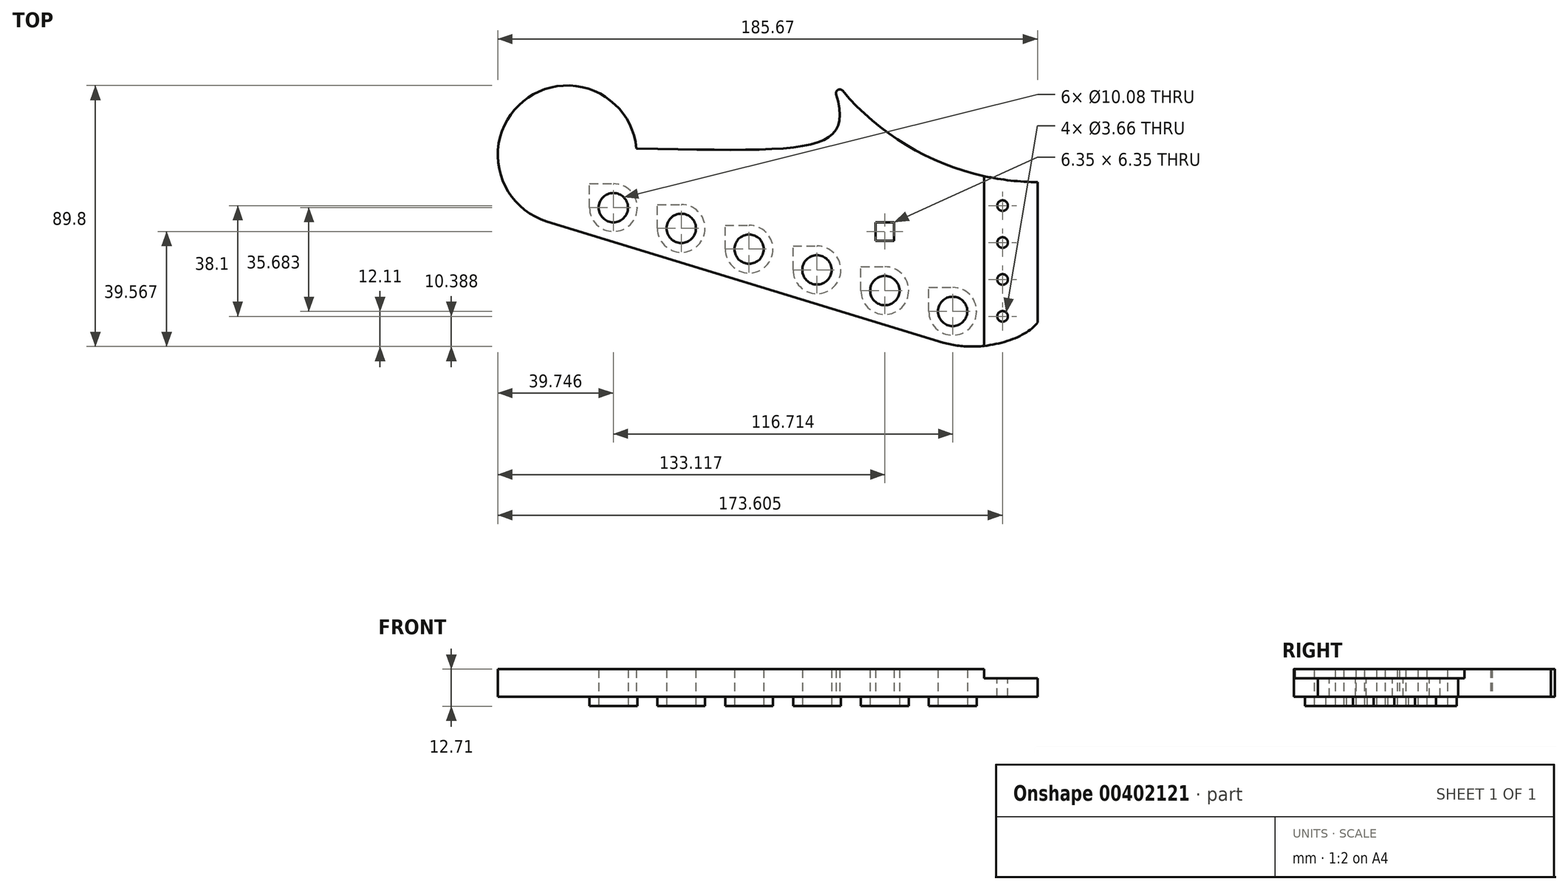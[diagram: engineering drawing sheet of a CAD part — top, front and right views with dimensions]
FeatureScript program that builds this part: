
annotation { "Feature Type Name" : "Feature", "Feature Type Description" : "" }
export const myFeature = defineFeature(function(context is Context, id is Id, definition is map)
    precondition{}
    {
        {
            var Q0;
            Q0=qCreatedBy(makeId("Top.planeOp"),FACE);
            var sketch = newSketch(context, id + "F0", { "sketchPlane" : qUnion([Q0])});
            skPoint(sketch, "E0", {"position": v(-185.67, 33.46) * mm});
            skLineSegment(sketch, "E1", {"start": v(0, 24.13) * mm, "end": v(0, -24.13) * mm});
            skCircle(sketch, "E2", {"center": v(-29.21, -20.32) * mm, "radius": 5.04 * mm});
            skLineSegment(sketch, "E3", {"start": v(0, 0) * mm, "end": v(0, 0) * mm});
            skPoint(sketch, "E3.endSnap0", {"position": v(0, 0) * mm});
            skCircle(sketch, "E4.1.0.0", {"center": v(-52.55, -13.18) * mm, "radius": 5.04 * mm});
            skCircle(sketch, "E4.2.0.0", {"center": v(-75.9, -6.05) * mm, "radius": 5.04 * mm});
            skCircle(sketch, "E4.3.0.0", {"center": v(-99.24, 1.09) * mm, "radius": 5.04 * mm});
            skCircle(sketch, "E4.4.0.0", {"center": v(-122.58, 8.23) * mm, "radius": 5.04 * mm});
            skCircle(sketch, "E4.5.0.0", {"center": v(-145.92, 15.36) * mm, "radius": 5.04 * mm});
            skLineSegment(sketch, "E4.direction1", {"start": v(-29.21, -20.32) * mm, "end": v(-52.55, -13.18) * mm, "construction": true});
            skLineSegment(sketch, "E5", {"start": v(-18.42, 26.22) * mm, "end": v(-18.41, -32.2) * mm});
            skLineSegment(sketch, "E6", {"start": v(-32.5, -31.06) * mm, "end": v(-168.76, 10.6) * mm});
            skLineSegment(sketch, "E7", {"start": v(-29.21, -20.32) * mm, "end": v(-32.5, -31.06) * mm, "construction": true});
            skFitSpline(sketch, "E8", {"points": [v(-32.5, -31.06) * mm, v(0, -24.13) * mm], "startDerivative": vector(36.44, -11.14) * mm, "endDerivative": vector(14.29, 19.05) * mm});
            skLineSegment(sketch, "E9", {"start": v(0, 0) * mm, "end": v(99.12, 0) * mm, "construction": true});
            skArc(sketch, "E10", {"start": v(-168.76, 10.6) * mm, "mid": v(-180.99, 19.25) * mm, "end": v(-185.67, 33.46) * mm});
            skLineSegment(sketch, "E11", {"start": v(-185.67, 33.46) * mm, "end": v(-185.67, 61.73) * mm, "construction": true});
            skArc(sketch, "E12", {"start": v(-137.98, 35.75) * mm, "mid": v(-162.91, 57.34) * mm, "end": v(-185.67, 33.46) * mm});
            skArc(sketch, "E13", {"start": v(-72.27, 62.33) * mm, "mid": v(-40.79, 34.43) * mm, "end": v(0, 24.13) * mm});
            skLineSegment(sketch, "E14", {"start": v(8.57, 3.57) * mm, "end": v(-99.24, 3.57) * mm, "construction": true});
            skLineSegment(sketch, "E15", {"start": v(8.57, -3.57) * mm, "end": v(-75.9, -3.57) * mm, "construction": true});
            skCircle(sketch, "E16", {"center": v(-75.9, -6.05) * mm, "radius": 2.48 * mm});
            skCircle(sketch, "E17", {"center": v(-99.24, 1.09) * mm, "radius": 2.48 * mm});
            skLineSegment(sketch, "E18", {"start": v(-99.24, 3.57) * mm, "end": v(-99.24, 1.09) * mm, "construction": true});
            skLineSegment(sketch, "E19", {"start": v(-75.9, -3.57) * mm, "end": v(-75.9, -6.05) * mm, "construction": true});
            skLineSegment(sketch, "E20", {"start": v(-137.98, 35.75) * mm, "end": v(-72.27, 62.33) * mm, "construction": true});
            skFitSpline(sketch, "E21", {"points": [v(-137.98, 35.75) * mm, v(-72.27, 62.33) * mm], "startDerivative": vector(194.61, -3.65) * mm, "endDerivative": vector(-37.72, 87.36) * mm});
            skCircle(sketch, "E22", {"center": v(-122.58, 8.23) * mm, "radius": 2.48 * mm});
            skCircle(sketch, "E23", {"center": v(-145.92, 15.36) * mm, "radius": 2.48 * mm});
            skLineSegment(sketch, "E24", {"start": v(-122.58, 8.23) * mm, "end": v(-122.58, 10.7) * mm});
            skLineSegment(sketch, "E25", {"start": v(-145.92, 15.36) * mm, "end": v(-145.92, 17.84) * mm});
            skLineSegment(sketch, "E26", {"start": v(-122.58, 10.7) * mm, "end": v(7.67, 10.7) * mm, "construction": true});
            skLineSegment(sketch, "E27", {"start": v(-145.92, 17.84) * mm, "end": v(21.7, 17.84) * mm, "construction": true});
            skSolve(sketch);
        }
        {
            var Q0;
            Q0=qSketchRegion(id+"F0",true);
            extrude(context, id + "F1", {"entities" : qUnion([Q0]), "depth" : 6.35 * mm});
        }
        {
            var Q0;
            Q0=makeQuery(id+"F0.imprint","IMPRINT",FACE,{"disambiguationData":[TD([[makeQuery(id+"F0.imprint","IMPRINT",EDGE,{"derivedFrom":sQuery(id+"F0.wireOp",EDGE,"E2")}),-1.0]])]});
            extrude(context, id + "F2", {"entities" : qUnion([Q0]), "operationType" : NewBodyOperationType.ADD, "depth" : 9.52 * mm});
        }
        {
            var Q0;
            Q0=makeQuery(id+"F1.opExtrude","CAP_FACE",FACE,{"disambiguationData":[OSD([sQuery(id+"F0.wireOp",EDGE,"4aa001a9-7916-4ac9-b611-f33505b9f3c5"),sQuery(id+"F0.wireOp",EDGE,"77602153-f705-4483-a7fc-31cc86b3ea61"),sQuery(id+"F0.wireOp",EDGE,"ee52411e-a9e7-4ef9-bd5f-1803b2297118"),sQuery(id+"F0.wireOp",EDGE,"E1"),sQuery(id+"F0.wireOp",EDGE,"E2"),sQuery(id+"F0.wireOp",EDGE,"E4.1.0.0"),sQuery(id+"F0.wireOp",EDGE,"E4.2.0.0"),sQuery(id+"F0.wireOp",EDGE,"E4.3.0.0"),sQuery(id+"F0.wireOp",EDGE,"E4.4.0.0"),sQuery(id+"F0.wireOp",EDGE,"E4.5.0.0"),sQuery(id+"F0.wireOp",EDGE,"05dfdfb5-9140-4733-bf36-b7656169c247"),sQuery(id+"F0.wireOp",EDGE,"fa98ec53-b239-455b-819f-4d27d42f24a3")])],"isStart":false});
            var sketch = newSketch(context, id + "F3", { "sketchPlane" : qUnion([Q0])});
            skPoint(sketch, "E28", {"position": v(-12.06, -22.04) * mm});
            skPoint(sketch, "E29", {"position": v(-12.06, 16.06) * mm});
            skPoint(sketch, "E30", {"position": v(-12.07, 3.36) * mm});
            skPoint(sketch, "E31", {"position": v(-12.06, -9.34) * mm});
            skLineSegment(sketch, "E32", {"start": v(0, -3) * mm, "end": v(-18.41, -3) * mm, "construction": true});
            skSolve(sketch);
        }
        {
            var Q0;
            Q0=sQuery(id+"F3.wireOp",VERTEX,"E29");
            var Q1;
            Q1=sQuery(id+"F3.wireOp",VERTEX,"E30");
            var Q2;
            Q2=sQuery(id+"F3.wireOp",VERTEX,"E31");
            var Q3;
            Q3=sQuery(id+"F3.wireOp",VERTEX,"E28");
            var Q4;
            Q4=makeQuery(id+"F1.opExtrude","SWEPT_BODY",BODY,{"disambiguationData":[OSD([sQuery(id+"F0.wireOp",EDGE,"4aa001a9-7916-4ac9-b611-f33505b9f3c5"),sQuery(id+"F0.wireOp",EDGE,"77602153-f705-4483-a7fc-31cc86b3ea61"),sQuery(id+"F0.wireOp",EDGE,"ee52411e-a9e7-4ef9-bd5f-1803b2297118"),sQuery(id+"F0.wireOp",EDGE,"E1"),sQuery(id+"F0.wireOp",EDGE,"E2"),sQuery(id+"F0.wireOp",EDGE,"E4.1.0.0"),sQuery(id+"F0.wireOp",EDGE,"E4.2.0.0"),sQuery(id+"F0.wireOp",EDGE,"E4.3.0.0"),sQuery(id+"F0.wireOp",EDGE,"E4.4.0.0"),sQuery(id+"F0.wireOp",EDGE,"E4.5.0.0"),sQuery(id+"F0.wireOp",EDGE,"05dfdfb5-9140-4733-bf36-b7656169c247"),sQuery(id+"F0.wireOp",EDGE,"fa98ec53-b239-455b-819f-4d27d42f24a3")])]});
            hole(context, id + "F4", {"style" : HoleStyle.SIMPLE, "endStyle" : HoleEndStyle.THROUGH, "standardTappedOrClearance" : lookupTablePath({ "standard" : "ANSI", "fit" : "Close", "size" : "#6", "type" : "Clearance" }), "standardBlindInLast" : lookupTablePath({ "fit" : "Close", "standard" : "ANSI", "size" : "#6", "type" : "Clearance" }), "holeDiameter" : 3.66 * mm, "startFromSketch" : true, "locations" : qUnion([Q0, Q1, Q2, Q3]), "scope" : qUnion([Q4]), "isTappedThrough" : true});
        }
        {
            var Q0;
            {var subQ0=sQuery(id+"F0.wireOp",EDGE,"E21");var subQ1=sQuery(id+"F0.wireOp",EDGE,"E13");Q0=makeQuery(id+"F2.boolean.opBoolean","MERGE",EDGE,{"derivedFrom":[makeQuery(id+"F1.opExtrude","SWEPT_EDGE",EDGE,{"disambiguationData":[OSD([subQ1,subQ0])]}),makeQuery(id+"F2.opExtrude","SWEPT_EDGE",EDGE,{"disambiguationData":[OSD([subQ1,subQ0])]})]});}
            fillet(context, id + "F5", {"entities" : qUnion([Q0]), "radius" : 1.27 * mm, "tangentPropagation" : true, "allowEdgeOverflow" : false});
        }
        {
            var Q0;
            Q0=makeQuery(id+"F2.opExtrude","CAP_FACE",FACE,{"disambiguationData":[OSD([sQuery(id+"F0.wireOp",EDGE,"E2"),sQuery(id+"F0.wireOp",EDGE,"E4.1.0.0"),sQuery(id+"F0.wireOp",EDGE,"E4.2.0.0"),sQuery(id+"F0.wireOp",EDGE,"E4.3.0.0"),sQuery(id+"F0.wireOp",EDGE,"E4.4.0.0"),sQuery(id+"F0.wireOp",EDGE,"E4.5.0.0"),sQuery(id+"F0.wireOp",EDGE,"E5"),sQuery(id+"F0.wireOp",EDGE,"E6"),sQuery(id+"F0.wireOp",EDGE,"E8"),sQuery(id+"F0.wireOp",EDGE,"E10"),sQuery(id+"F0.wireOp",EDGE,"E12"),sQuery(id+"F0.wireOp",EDGE,"E13"),sQuery(id+"F0.wireOp",EDGE,"E21")])],"isStart":false});
            var sketch = newSketch(context, id + "F6", { "sketchPlane" : qUnion([Q0])});
            skArc(sketch, "E33", {"start": v(-176.02, 0) * mm, "mid": v(-95.34, 4.1) * mm, "end": v(-40.97, 63.86) * mm});
            skArc(sketch, "E34.0", {"start": v(-172.8, 9.1) * mm, "mid": v(-99.46, 12.82) * mm, "end": v(-50.05, 67.14) * mm});
            skArc(sketch, "E35", {"start": v(-33.84, 84.78) * mm, "mid": v(-42.65, 23.63) * mm, "end": v(-29.69, -36.76) * mm});
            skArc(sketch, "E36.0", {"start": v(-38.9, 86.46) * mm, "mid": v(-47.98, 23.45) * mm, "end": v(-34.62, -38.79) * mm});
            skArc(sketch, "E37", {"start": v(-118.56, -20.84) * mm, "mid": v(-145.78, 28.3) * mm, "end": v(-199.55, 44.5) * mm});
            skArc(sketch, "E38.0", {"start": v(-108.22, -19.6) * mm, "mid": v(-139.24, 36.4) * mm, "end": v(-200.52, 54.87) * mm});
            skLineSegment(sketch, "E39.0", {"start": v(-32.5, -31.06) * mm, "end": v(-168.76, 10.6) * mm});
            skArc(sketch, "E39.1", {"start": v(-137.98, 35.75) * mm, "mid": v(-176.9, 51.98) * mm, "end": v(-168.76, 10.6) * mm});
            skFitSpline(sketch, "E39.2", {"points": [v(-137.98, 35.75) * mm, v(-73.1, 34.53) * mm, v(-60.64, 33.21) * mm, v(-73.21, 62.33) * mm]});
            skArc(sketch, "E39.3", {"start": v(-67.1, 55.59) * mm, "mid": v(-68.68, 55.88) * mm, "end": v(-69.28, 54.4) * mm});
            skArc(sketch, "E39.4", {"start": v(-67.1, 55.59) * mm, "mid": v(-45.17, 36.9) * mm, "end": v(-18.41, 26.22) * mm});
            skFitSpline(sketch, "E39.5", {"points": [v(-32.5, -31.06) * mm, v(-20.35, -34.77) * mm, v(-4.76, -30.48) * mm, v(0, -24.13) * mm]});
            skLineSegment(sketch, "E39.6", {"start": v(-18.42, 26.22) * mm, "end": v(-18.41, -32.2) * mm});
            skSolve(sketch);
        }
        {
            var Q0;
            Q0=makeQuery(id+"F2.opExtrude","CAP_FACE",FACE,{"disambiguationData":[OSD([sQuery(id+"F0.wireOp",EDGE,"E2"),sQuery(id+"F0.wireOp",EDGE,"E4.1.0.0"),sQuery(id+"F0.wireOp",EDGE,"E4.2.0.0"),sQuery(id+"F0.wireOp",EDGE,"E4.3.0.0"),sQuery(id+"F0.wireOp",EDGE,"E4.4.0.0"),sQuery(id+"F0.wireOp",EDGE,"E4.5.0.0"),sQuery(id+"F0.wireOp",EDGE,"E5"),sQuery(id+"F0.wireOp",EDGE,"E6"),sQuery(id+"F0.wireOp",EDGE,"E8"),sQuery(id+"F0.wireOp",EDGE,"E10"),sQuery(id+"F0.wireOp",EDGE,"E12"),sQuery(id+"F0.wireOp",EDGE,"E13"),sQuery(id+"F0.wireOp",EDGE,"E21")])],"isStart":false});
            var sketch = newSketch(context, id + "F7", { "sketchPlane" : qUnion([Q0])});
            skLineSegment(sketch, "E40", {"start": v(-13.49, 50.46) * mm, "end": v(-120.4, -45.77) * mm});
            skLineSegment(sketch, "E41", {"start": v(-120.4, -45.77) * mm, "end": v(-124.32, -41.42) * mm});
            skLineSegment(sketch, "E42", {"start": v(-124.32, -41.42) * mm, "end": v(-17.2, 55) * mm});
            skLineSegment(sketch, "E43", {"start": v(-17.2, 55) * mm, "end": v(-13.49, 50.46) * mm});
            skLineSegment(sketch, "E44", {"start": v(-49.09, -54.74) * mm, "end": v(-69.94, 75.3) * mm});
            skLineSegment(sketch, "E45", {"start": v(-69.94, 75.3) * mm, "end": v(-75.5, 74.4) * mm});
            skLineSegment(sketch, "E46", {"start": v(-75.5, 74.4) * mm, "end": v(-54.41, -57.09) * mm});
            skLineSegment(sketch, "E47", {"start": v(-54.41, -57.09) * mm, "end": v(-49.09, -54.74) * mm});
            skLineSegment(sketch, "E48", {"start": v(-151.73, -17.56) * mm, "end": v(37.22, 6.84) * mm});
            skLineSegment(sketch, "E49", {"start": v(37.22, 6.84) * mm, "end": v(35.94, 14.83) * mm});
            skLineSegment(sketch, "E50", {"start": v(35.94, 14.83) * mm, "end": v(-152.1, -9.45) * mm});
            skLineSegment(sketch, "E51", {"start": v(-152.1, -9.45) * mm, "end": v(-151.73, -17.56) * mm});
            skLineSegment(sketch, "E52", {"start": v(-167.26, 91.8) * mm, "end": v(-135.04, -31.2) * mm});
            skLineSegment(sketch, "E53", {"start": v(-135.04, -31.2) * mm, "end": v(-143.78, -33.49) * mm});
            skLineSegment(sketch, "E54", {"start": v(-143.78, -33.49) * mm, "end": v(-175.54, 87.77) * mm});
            skLineSegment(sketch, "E55", {"start": v(-175.54, 87.77) * mm, "end": v(-167.26, 91.8) * mm});
            skLineSegment(sketch, "E56", {"start": v(-107.47, 85.6) * mm, "end": v(-120.17, 6.32) * mm});
            skLineSegment(sketch, "E57", {"start": v(-120.17, 6.32) * mm, "end": v(-125.36, 7.15) * mm});
            skLineSegment(sketch, "E58", {"start": v(-125.36, 7.15) * mm, "end": v(-112.55, 87.16) * mm});
            skLineSegment(sketch, "E59", {"start": v(-112.55, 87.16) * mm, "end": v(-107.47, 85.6) * mm});
            skLineSegment(sketch, "E60", {"start": v(-28.5, -37.42) * mm, "end": v(-138.14, 44.12) * mm});
            skLineSegment(sketch, "E61", {"start": v(-138.14, 44.12) * mm, "end": v(-135.1, 48.2) * mm});
            skLineSegment(sketch, "E62", {"start": v(-135.1, 48.2) * mm, "end": v(-25, -33.69) * mm});
            skLineSegment(sketch, "E63", {"start": v(-25, -33.69) * mm, "end": v(-28.5, -37.42) * mm});
            skLineSegment(sketch, "E64", {"start": v(-38.7, 46.06) * mm, "end": v(-209.58, 10.9) * mm});
            skLineSegment(sketch, "E65", {"start": v(-209.58, 10.9) * mm, "end": v(-211.15, 18.56) * mm});
            skLineSegment(sketch, "E66", {"start": v(-211.15, 18.56) * mm, "end": v(-40.21, 53.74) * mm});
            skLineSegment(sketch, "E67", {"start": v(-40.21, 53.74) * mm, "end": v(-38.7, 46.06) * mm});
            skText(sketch, "E68", { "text": "Bernstein", "fontName": "NotoSerif-Italic.ttf"});
            const initialGuessF7  = {"E68": [-0.0729, 0.03836, -0.97948, -0.20155, 0.00547]};
            skSetInitialGuess(sketch, initialGuessF7);
            skSolve(sketch);
        }
        {
            var Q0;
            Q0=qCreatedBy(makeId("Top.planeOp"),FACE);
            var sketch = newSketch(context, id + "F8", { "sketchPlane" : qUnion([Q0])});
            skLineSegment(sketch, "E69.0", {"start": v(-122.58, 10.7) * mm, "end": v(7.67, 10.7) * mm, "construction": true});
            skLineSegment(sketch, "E69.1", {"start": v(-145.92, 17.84) * mm, "end": v(21.7, 17.84) * mm, "construction": true});
            skLineSegment(sketch, "E70.bottom", {"start": v(-49.38, 3.96) * mm, "end": v(-55.73, 3.96) * mm});
            skLineSegment(sketch, "E70.top", {"start": v(-49.38, 10.31) * mm, "end": v(-55.73, 10.31) * mm});
            skLineSegment(sketch, "E70.left", {"start": v(-49.38, 3.96) * mm, "end": v(-49.38, 10.31) * mm});
            skLineSegment(sketch, "E70.right", {"start": v(-55.73, 3.96) * mm, "end": v(-55.73, 10.31) * mm});
            skPoint(sketch, "E70.middle", {"position": v(-52.55, 7.14) * mm});
            skLineSegment(sketch, "E71.0", {"start": v(8.57, 3.57) * mm, "end": v(-99.24, 3.57) * mm, "construction": true});
            skLineSegment(sketch, "E72", {"start": v(-52.55, 7.14) * mm, "end": v(-66.43, 7.14) * mm, "construction": true});
            skPoint(sketch, "E73", {"position": v(-52.55, -13.18) * mm});
            skSolve(sketch);
        }
        {
            var Q0;
            Q0=qSketchRegion(id+"F8",true);
            extrude(context, id + "F9", {"entities" : qUnion([Q0]), "operationType" : NewBodyOperationType.REMOVE, "endBound" : BoundingType.THROUGH_ALL, "depth" : 25.4 * mm});
        }
        {
            var Q0;
            Q0=makeQuery(id+"F1.opExtrude","CAP_FACE",FACE,{"disambiguationData":[OSD([sQuery(id+"F0.wireOp",EDGE,"E1"),sQuery(id+"F0.wireOp",EDGE,"E2"),sQuery(id+"F0.wireOp",EDGE,"E4.1.0.0"),sQuery(id+"F0.wireOp",EDGE,"E4.2.0.0"),sQuery(id+"F0.wireOp",EDGE,"E4.3.0.0"),sQuery(id+"F0.wireOp",EDGE,"E4.4.0.0"),sQuery(id+"F0.wireOp",EDGE,"E4.5.0.0"),sQuery(id+"F0.wireOp",EDGE,"E6"),sQuery(id+"F0.wireOp",EDGE,"E8"),sQuery(id+"F0.wireOp",EDGE,"E10"),sQuery(id+"F0.wireOp",EDGE,"E12"),sQuery(id+"F0.wireOp",EDGE,"E13"),sQuery(id+"F0.wireOp",EDGE,"E21")])],"isStart":true});
            var sketch = newSketch(context, id + "F10", { "sketchPlane" : qUnion([Q0])});
            skCircle(sketch, "E74.0", {"center": v(-29.21, 20.32) * mm, "radius": 5.04 * mm});
            skCircle(sketch, "E75.0", {"center": v(-29.21, 20.32) * mm, "radius": 8.22 * mm});
            skLineSegment(sketch, "E76", {"start": v(-37.43, 20.32) * mm, "end": v(-37.43, 12.1) * mm});
            skLineSegment(sketch, "E77", {"start": v(-37.43, 12.1) * mm, "end": v(-29.21, 12.1) * mm});
            skLineSegment(sketch, "E78", {"start": v(-29.2, 20.32) * mm, "end": v(-52.55, 13.18) * mm, "construction": true});
            skLineSegment(sketch, "E79.1.0.0", {"start": v(-60.77, 13.18) * mm, "end": v(-60.77, 4.97) * mm});
            skLineSegment(sketch, "E79.1.0.1", {"start": v(-60.77, 4.97) * mm, "end": v(-52.55, 4.97) * mm});
            skCircle(sketch, "E79.1.0.2", {"center": v(-52.55, 13.18) * mm, "radius": 8.22 * mm});
            skCircle(sketch, "E79.1.0.3", {"center": v(-52.55, 13.18) * mm, "radius": 5.04 * mm});
            skLineSegment(sketch, "E79.2.0.0", {"start": v(-84.11, 6.05) * mm, "end": v(-84.11, -2.17) * mm});
            skLineSegment(sketch, "E79.2.0.1", {"start": v(-84.11, -2.17) * mm, "end": v(-75.9, -2.17) * mm});
            skCircle(sketch, "E79.2.0.2", {"center": v(-75.9, 6.05) * mm, "radius": 8.22 * mm});
            skCircle(sketch, "E79.2.0.3", {"center": v(-75.9, 6.05) * mm, "radius": 5.04 * mm});
            skLineSegment(sketch, "E79.3.0.0", {"start": v(-107.46, -1.09) * mm, "end": v(-107.46, -9.3) * mm});
            skLineSegment(sketch, "E79.3.0.1", {"start": v(-107.46, -9.3) * mm, "end": v(-99.24, -9.3) * mm});
            skCircle(sketch, "E79.3.0.2", {"center": v(-99.24, -1.09) * mm, "radius": 8.22 * mm});
            skCircle(sketch, "E79.3.0.3", {"center": v(-99.24, -1.09) * mm, "radius": 5.04 * mm});
            skLineSegment(sketch, "E79.4.0.0", {"start": v(-130.8, -8.23) * mm, "end": v(-130.8, -16.44) * mm});
            skLineSegment(sketch, "E79.4.0.1", {"start": v(-130.8, -16.44) * mm, "end": v(-122.58, -16.44) * mm});
            skCircle(sketch, "E79.4.0.2", {"center": v(-122.58, -8.23) * mm, "radius": 8.22 * mm});
            skCircle(sketch, "E79.4.0.3", {"center": v(-122.58, -8.23) * mm, "radius": 5.04 * mm});
            skLineSegment(sketch, "E79.5.0.0", {"start": v(-154.14, -15.36) * mm, "end": v(-154.14, -23.58) * mm});
            skLineSegment(sketch, "E79.5.0.1", {"start": v(-154.14, -23.58) * mm, "end": v(-145.92, -23.58) * mm});
            skCircle(sketch, "E79.5.0.2", {"center": v(-145.92, -15.36) * mm, "radius": 8.22 * mm});
            skCircle(sketch, "E79.5.0.3", {"center": v(-145.92, -15.36) * mm, "radius": 5.04 * mm});
            skSolve(sketch);
        }
        {
            var Q0;
            Q0=qSketchRegion(id+"F10",true);
            extrude(context, id + "F11", {"entities" : qUnion([Q0]), "operationType" : NewBodyOperationType.ADD, "depth" : 3.17 * mm});
        }
    });
